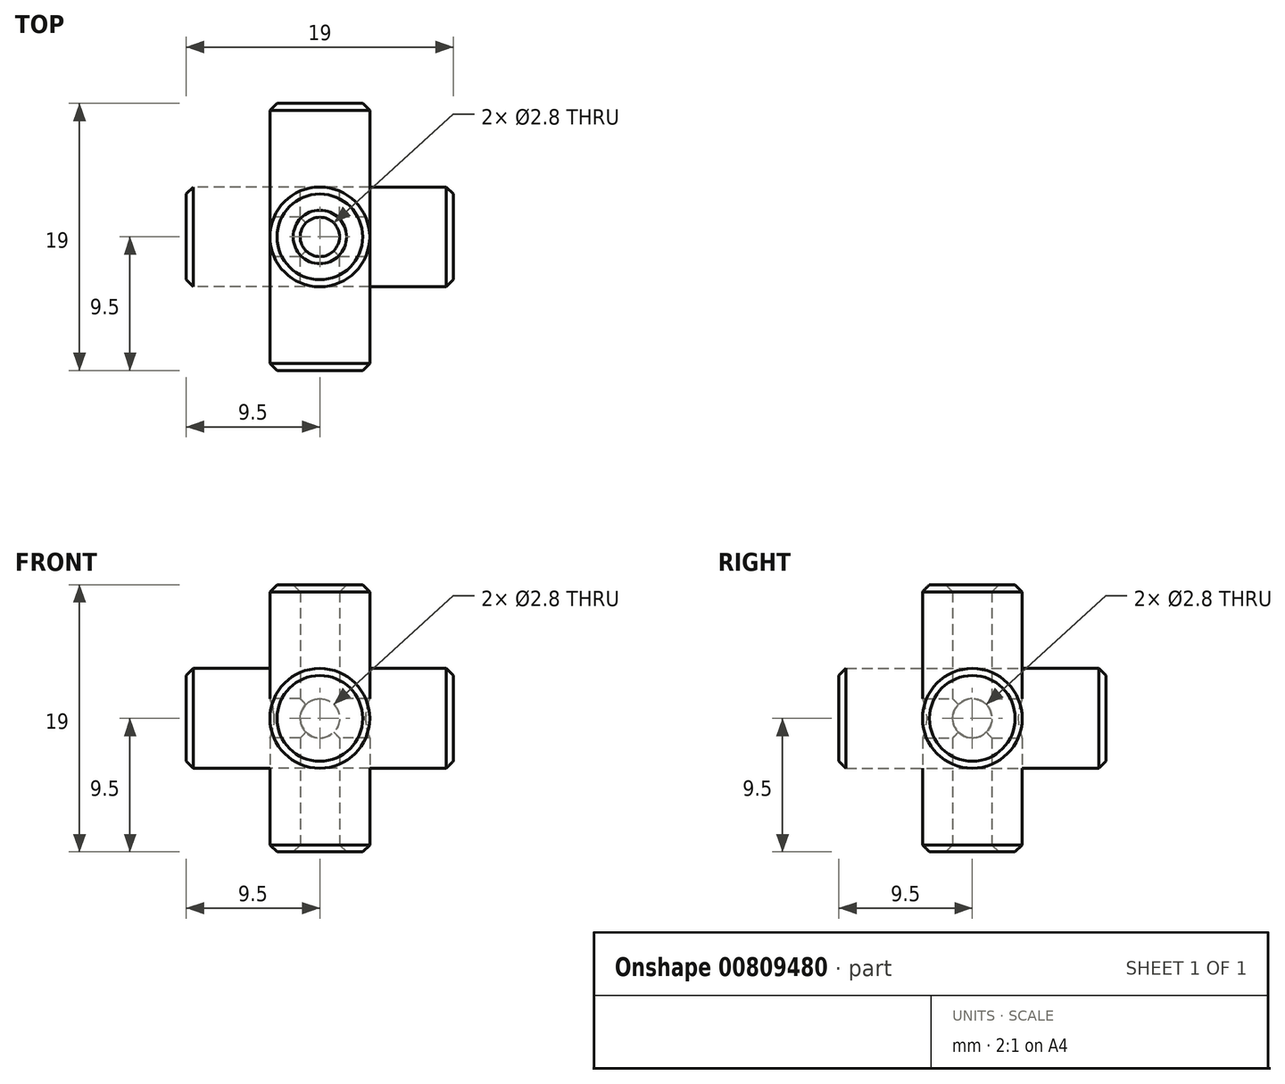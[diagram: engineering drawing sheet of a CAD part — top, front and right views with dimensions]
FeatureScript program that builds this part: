
annotation { "Feature Type Name" : "Feature", "Feature Type Description" : "" }
export const myFeature = defineFeature(function(context is Context, id is Id, definition is map)
    precondition{}
    {
        {
            var Q0;
            Q0=qCreatedBy(makeId("Front.planeOp"),FACE);
            var sketch = newSketch(context, id + "F0", { "sketchPlane" : qUnion([Q0])});
            skCircle(sketch, "E0", {"center": v(0, 0) * mm, "radius": 3.55 * mm});
            skSolve(sketch);
        }
        {
            var Q0;
            Q0 = qSketchRegion(id + "F0", true);
            extrude(context, id + "F1", {"entities" : qUnion([Q0]), "endBound" : BoundingType.SYMMETRIC, "depth" : 19 * mm, "offsetDistance" : 25 * mm});
        }
        {
            var Q0;
            Q0=qCreatedBy(makeId("Front.planeOp"),FACE);
            var sketch = newSketch(context, id + "F2", { "sketchPlane" : qUnion([Q0])});
            skCircle(sketch, "E1", {"center": v(0, 0) * mm, "radius": 1.4 * mm});
            skSolve(sketch);
        }
        {
            var Q0;
            Q0 = qSketchRegion(id + "F2", true);
            extrude(context, id + "F3", {"entities" : qUnion([Q0]), "endBound" : BoundingType.SYMMETRIC, "depth" : 20 * mm, "offsetDistance" : 25 * mm});
        }
        {
            var Q0;
            Q0=qCreatedBy(makeId("Front.planeOp"),FACE);
            var sketch = newSketch(context, id + "F4", { "sketchPlane" : qUnion([Q0])});
            skLineSegment(sketch, "E2.bottom", {"start": v(0, 0) * mm, "end": v(10, 0) * mm});
            skLineSegment(sketch, "E2.top", {"start": v(0, 10) * mm, "end": v(10, 10) * mm});
            skLineSegment(sketch, "E2.left", {"start": v(0, 0) * mm, "end": v(0, 10) * mm});
            skLineSegment(sketch, "E2.right", {"start": v(10, 0) * mm, "end": v(10, 10) * mm});
            skSolve(sketch);
        }
        {
            var Q0;
            Q0 = qSketchRegion(id + "F4", true);
            extrude(context, id + "F5", {"entities" : qUnion([Q0]), "depth" : 10 * mm, "offsetDistance" : 25 * mm});
        }
        {
            var Q0;
            Q0=qCreatedBy(makeId("Origin.pointOp"),VERTEX);
            var Q1;
            Q1=makeQuery(id+"F5.opExtrude","CAP_VERTEX",VERTEX,{"disambiguationData":[OSD([sQuery(id+"F4.wireOp",EDGE,"E2.top"),sQuery(id+"F4.wireOp",EDGE,"E2.right")])],"isStart":false});
            var Q2;
            Q2=makeQuery(id+"F5.opExtrude","CAP_VERTEX",VERTEX,{"disambiguationData":[OSD([sQuery(id+"F4.wireOp",EDGE,"E2.bottom"),sQuery(id+"F4.wireOp",EDGE,"E2.right")])],"isStart":false});
            cPlane(context, id + "F6", {"entities" : qUnion([Q0, Q1, Q2]), "cplaneType" : CPlaneType.THREE_POINT, "offset" : 25 * mm, "width" : 150 * mm, "height" : 150 * mm});
        }
        {
            var Q0;
            Q0=qCreatedBy(id+"F6.planeOp",FACE);
            var sketch = newSketch(context, id + "F7", { "sketchPlane" : qUnion([Q0])});
            skLineSegment(sketch, "E3", {"start": v(0, 0) * mm, "end": v(14.14, 10) * mm});
            skSolve(sketch);
        }
        {
            var Q0;
            Q0=makeQuery(id+"F5.opExtrude","SWEPT_BODY",BODY,{"disambiguationData":[OSD([sQuery(id+"F4.wireOp",EDGE,"E2.bottom"),sQuery(id+"F4.wireOp",EDGE,"E2.top"),sQuery(id+"F4.wireOp",EDGE,"E2.left"),sQuery(id+"F4.wireOp",EDGE,"E2.right")])]});
            deleteBodies(context, id + "F8", {"entities" : qUnion([Q0])});
        }
        {
            var Q0;
            Q0=makeQuery(id+"F1.opExtrude","SWEPT_BODY",BODY,{"disambiguationData":[OSD([sQuery(id+"F0.wireOp",EDGE,"E0")])]});
            var Q1;
            Q1=makeQuery(id+"F3.opExtrude","SWEPT_BODY",BODY,{"disambiguationData":[OSD([sQuery(id+"F2.wireOp",EDGE,"E1")])]});
            var Q2;
            Q2=sQuery(id+"F7.wireOp",EDGE,"E3");
            circularPattern(context, id + "F9", {"entities" : qUnion([Q0, Q1]), "axis" : qUnion([Q2]), "angle" : 360 * degree, "instanceCount" : 3, "equalSpace" : true});
        }
        {
            var Q0;
            Q0=makeQuery(id+"F9.opPattern","COPY",BODY,{"derivedFrom":makeQuery(id+"F3.opExtrude","SWEPT_BODY",BODY,{"disambiguationData":[OSD([sQuery(id+"F2.wireOp",EDGE,"E1")])]}),"instanceName":"2"});
            var Q1;
            Q1=makeQuery(id+"F9.opPattern","COPY",BODY,{"derivedFrom":makeQuery(id+"F3.opExtrude","SWEPT_BODY",BODY,{"disambiguationData":[OSD([sQuery(id+"F2.wireOp",EDGE,"E1")])]}),"instanceName":"1"});
            var Q2;
            Q2=makeQuery(id+"F3.opExtrude","SWEPT_BODY",BODY,{"disambiguationData":[OSD([sQuery(id+"F2.wireOp",EDGE,"E1")])]});
            var Q3;
            Q3=makeQuery(id+"F9.opPattern","COPY",BODY,{"derivedFrom":makeQuery(id+"F1.opExtrude","SWEPT_BODY",BODY,{"disambiguationData":[OSD([sQuery(id+"F0.wireOp",EDGE,"E0")])]}),"instanceName":"2"});
            booleanBodies(context, id + "F10", {"operationType" : BooleanOperationType.SUBTRACTION, "tools" : qUnion([Q0, Q1, Q2]), "targets" : qUnion([Q3])});
        }
        {
            var Q0;
            Q0=makeQuery(id+"F9.opPattern","COPY",EDGE,{"derivedFrom":makeQuery(id+"F1.opExtrude","CAP_EDGE",EDGE,{"disambiguationData":[OSD([sQuery(id+"F0.wireOp",EDGE,"E0")])],"isStart":false}),"instanceName":"2"});
            var Q1;
            Q1=makeQuery(id+"F10.opBoolean","INTERSECT",EDGE,{"derivedFrom":[makeQuery(id+"F9.opPattern","COPY",FACE,{"derivedFrom":makeQuery(id+"F1.opExtrude","CAP_FACE",FACE,{"disambiguationData":[OSD([sQuery(id+"F0.wireOp",EDGE,"E0")])],"isStart":false}),"instanceName":"2"}),makeQuery(id+"F9.opPattern","COPY",FACE,{"derivedFrom":makeQuery(id+"F3.opExtrude","SWEPT_FACE",FACE,{"disambiguationData":[OSD([sQuery(id+"F2.wireOp",EDGE,"E1")])]}),"instanceName":"2"})]});
            var Q2;
            Q2=makeQuery(id+"F10.opBoolean","INTERSECT",EDGE,{"derivedFrom":[makeQuery(id+"F1.opExtrude","CAP_FACE",FACE,{"disambiguationData":[OSD([sQuery(id+"F0.wireOp",EDGE,"E0")])],"isStart":false}),makeQuery(id+"F3.opExtrude","SWEPT_FACE",FACE,{"disambiguationData":[OSD([sQuery(id+"F2.wireOp",EDGE,"E1")])]})]});
            var Q3;
            Q3=makeQuery(id+"F1.opExtrude","CAP_FACE",FACE,{"disambiguationData":[OSD([sQuery(id+"F0.wireOp",EDGE,"E0")])],"isStart":false});
            var Q4;
            Q4=makeQuery(id+"F9.opPattern","COPY",FACE,{"derivedFrom":makeQuery(id+"F1.opExtrude","CAP_FACE",FACE,{"disambiguationData":[OSD([sQuery(id+"F0.wireOp",EDGE,"E0")])],"isStart":true}),"instanceName":"1"});
            var Q5;
            Q5=makeQuery(id+"F1.opExtrude","CAP_FACE",FACE,{"disambiguationData":[OSD([sQuery(id+"F0.wireOp",EDGE,"E0")])],"isStart":true});
            var Q6;
            Q6=makeQuery(id+"F9.opPattern","COPY",FACE,{"derivedFrom":makeQuery(id+"F1.opExtrude","CAP_FACE",FACE,{"disambiguationData":[OSD([sQuery(id+"F0.wireOp",EDGE,"E0")])],"isStart":false}),"instanceName":"1"});
            var Q7;
            Q7=makeQuery(id+"F9.opPattern","COPY",FACE,{"derivedFrom":makeQuery(id+"F1.opExtrude","CAP_FACE",FACE,{"disambiguationData":[OSD([sQuery(id+"F0.wireOp",EDGE,"E0")])],"isStart":true}),"instanceName":"2"});
            chamfer(context, id + "F11", {"entities" : qUnion([Q0, Q1, Q2, Q3, Q4, Q5, Q6, Q7]), "width" : 0.5 * mm, "tangentPropagation" : true});
        }
    });
